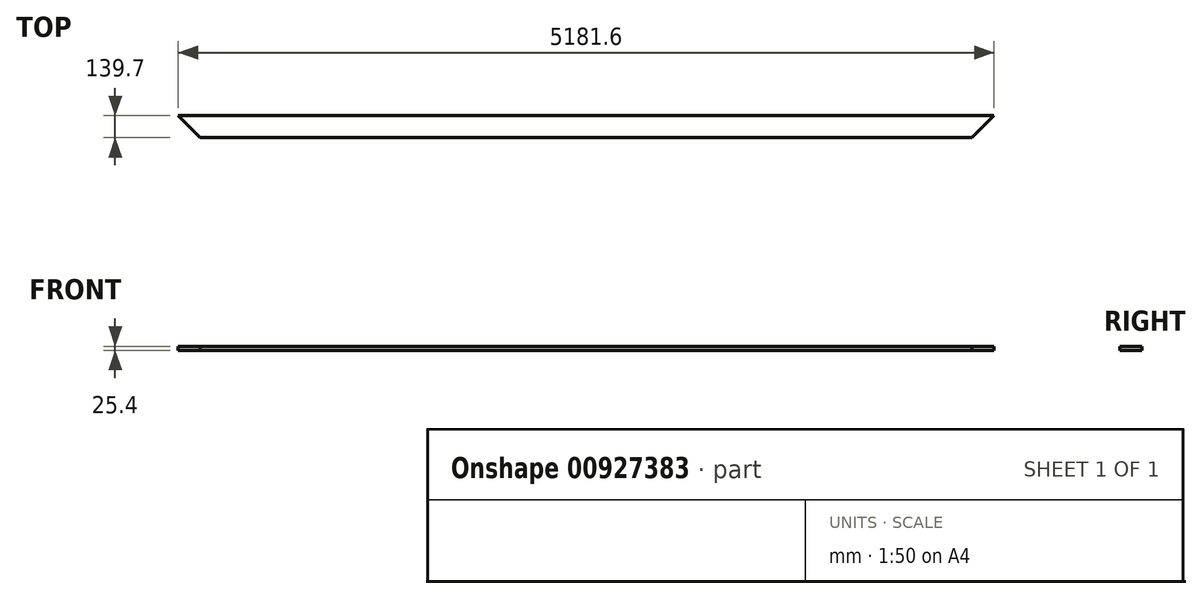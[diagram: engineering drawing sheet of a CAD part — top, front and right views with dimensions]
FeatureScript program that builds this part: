
annotation { "Feature Type Name" : "Feature", "Feature Type Description" : "" }
export const myFeature = defineFeature(function(context is Context, id is Id, definition is map)
    precondition{}
    {
        {
            var Q0;
            Q0=qCreatedBy(makeId("Top.planeOp"),FACE);
            var sketch = newSketch(context, id + "F0", { "sketchPlane" : qUnion([Q0])});
            skLineSegment(sketch, "E0", {"start": v(-2590.8, 69.85) * mm, "end": v(2590.8, 69.85) * mm});
            skLineSegment(sketch, "E1", {"start": v(2590.8, 69.85) * mm, "end": v(2451.1, -69.85) * mm});
            skLineSegment(sketch, "E2", {"start": v(2451.1, -69.85) * mm, "end": v(-2451.1, -69.85) * mm});
            skLineSegment(sketch, "E3", {"start": v(-2451.1, -69.85) * mm, "end": v(-2590.8, 69.85) * mm});
            skSolve(sketch);
        }
        {
            var Q0;
            Q0 = qSketchRegion(id + "F0", true);
            extrude(context, id + "F1", {"entities" : qUnion([Q0]), "depth" : 25.4 * mm, "offsetDistance" : 25.4 * mm});
        }
    });
